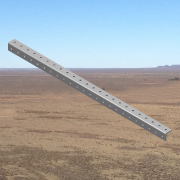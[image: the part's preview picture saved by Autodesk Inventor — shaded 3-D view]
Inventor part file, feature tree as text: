
AUTODESK INVENTOR PART (.ipt)
format: ipt  version: 2014 SP1 (Build 180222100, 222)  size: 188,416 bytes
history: native  units: in
note: dims shown in document units (in); Inventor stores cm internally (conversion verified against a paired STEP export)
features: sketch x3, hole x2, pattern_linear x2, extrude x1
ambient origin geometry x8: Origin, YZ Plane, XZ Plane, XY Plane, X Axis, Y Axis, Z Axis, Center Point
bodies: Solid1 (feature_tree)
feature tree (8):
  extrude  "Extrusion1"  Depth=1.0in
  hole  "Hole1"  [1 undecoded]
  pattern_linear  "Rectangular Pattern1"  Count1=24 Spacing1=1.0in
  hole  "Hole2"  [1 undecoded]
  pattern_linear  "Rectangular Pattern2"  Count1=24 Spacing1=1.0in
  sketch  "Sketch1"  dims[d0=1.0in d1=1.0in]
  sketch  "Sketch2"  dims[d2=0.125in d3=24.0in d4=0.0in]
  sketch  "Sketch3"  dims[d5=0.5in d6=0.25in d7=0.75in d8=0.375in d9=0.25in d10=0.5635in d11=1.0in d12=0.8108in d13=9.4488in d15=1.0in d16=0.5in d17=0.25in d18=0.75in d19=0.375in d20=0.25in d21=0.5635in d22=1.0in d23=0.8108in d24=9.4488in d26=1.0in]
note: 2 required parameter values undecoded (feature->parameter linkage not recoverable at this tier; creation-order binding heuristic only, values carry confidence <= 0.55)
